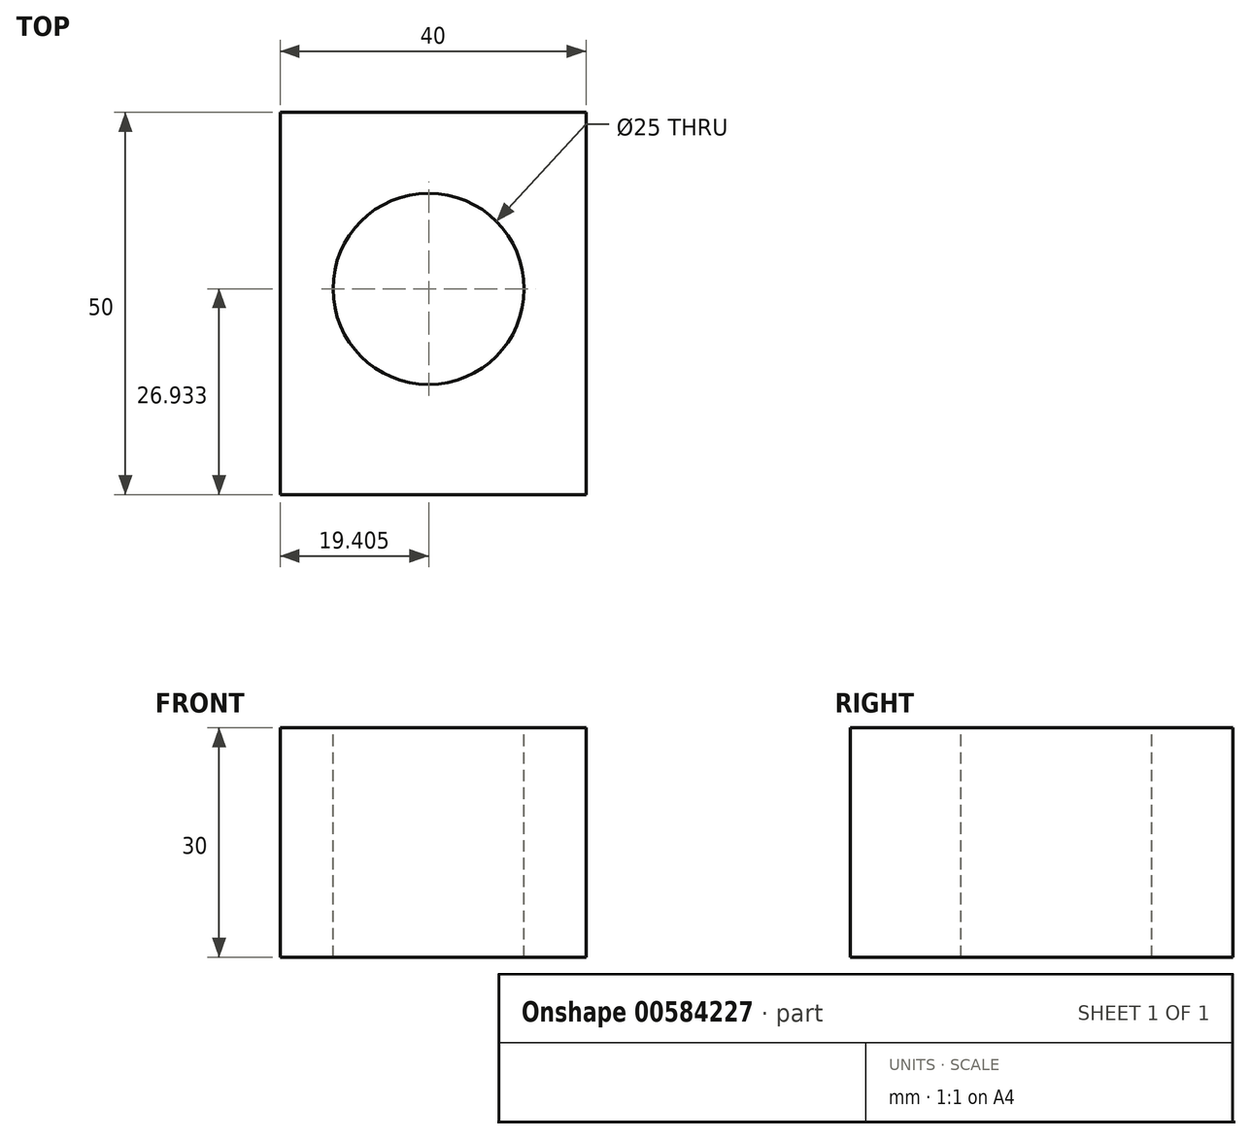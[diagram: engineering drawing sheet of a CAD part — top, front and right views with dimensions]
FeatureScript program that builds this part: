
annotation { "Feature Type Name" : "Feature", "Feature Type Description" : "" }
export const myFeature = defineFeature(function(context is Context, id is Id, definition is map)
    precondition{}
    {
        {
            var Q0;
            Q0=qCreatedBy(makeId("Front.planeOp"),FACE);
            var sketch = newSketch(context, id + "F0", { "sketchPlane" : qUnion([Q0])});
            skLineSegment(sketch, "E0.bottom", {"start": v(0, 0) * mm, "end": v(40, 0) * mm});
            skLineSegment(sketch, "E0.top", {"start": v(0, 30) * mm, "end": v(40, 30) * mm});
            skLineSegment(sketch, "E0.left", {"start": v(0, 0) * mm, "end": v(0, 30) * mm});
            skLineSegment(sketch, "E0.right", {"start": v(40, 0) * mm, "end": v(40, 30) * mm});
            skSolve(sketch);
        }
        {
            var Q0;
            Q0 = qSketchRegion(id + "F0", true);
            extrude(context, id + "F1", {"entities" : qUnion([Q0]), "depth" : 50 * mm, "offsetDistance" : 25 * mm});
        }
        {
            var Q0;
            Q0=makeQuery(id+"F1.opExtrude","SWEPT_FACE",FACE,{"disambiguationData":[OSD([sQuery(id+"F0.wireOp",EDGE,"E0.top")])]});
            var sketch = newSketch(context, id + "F2", { "sketchPlane" : qUnion([Q0])});
            skCircle(sketch, "E1", {"center": v(19.4, -23.07) * mm, "radius": 12.5 * mm});
            skSolve(sketch);
        }
        {
            var Q0;
            Q0 = qSketchRegion(id + "F2", true);
            extrude(context, id + "F3", {"entities" : qUnion([Q0]), "operationType" : NewBodyOperationType.REMOVE, "oppositeDirection" : true, "depth" : 30 * mm, "offsetDistance" : 25 * mm});
        }
    });
